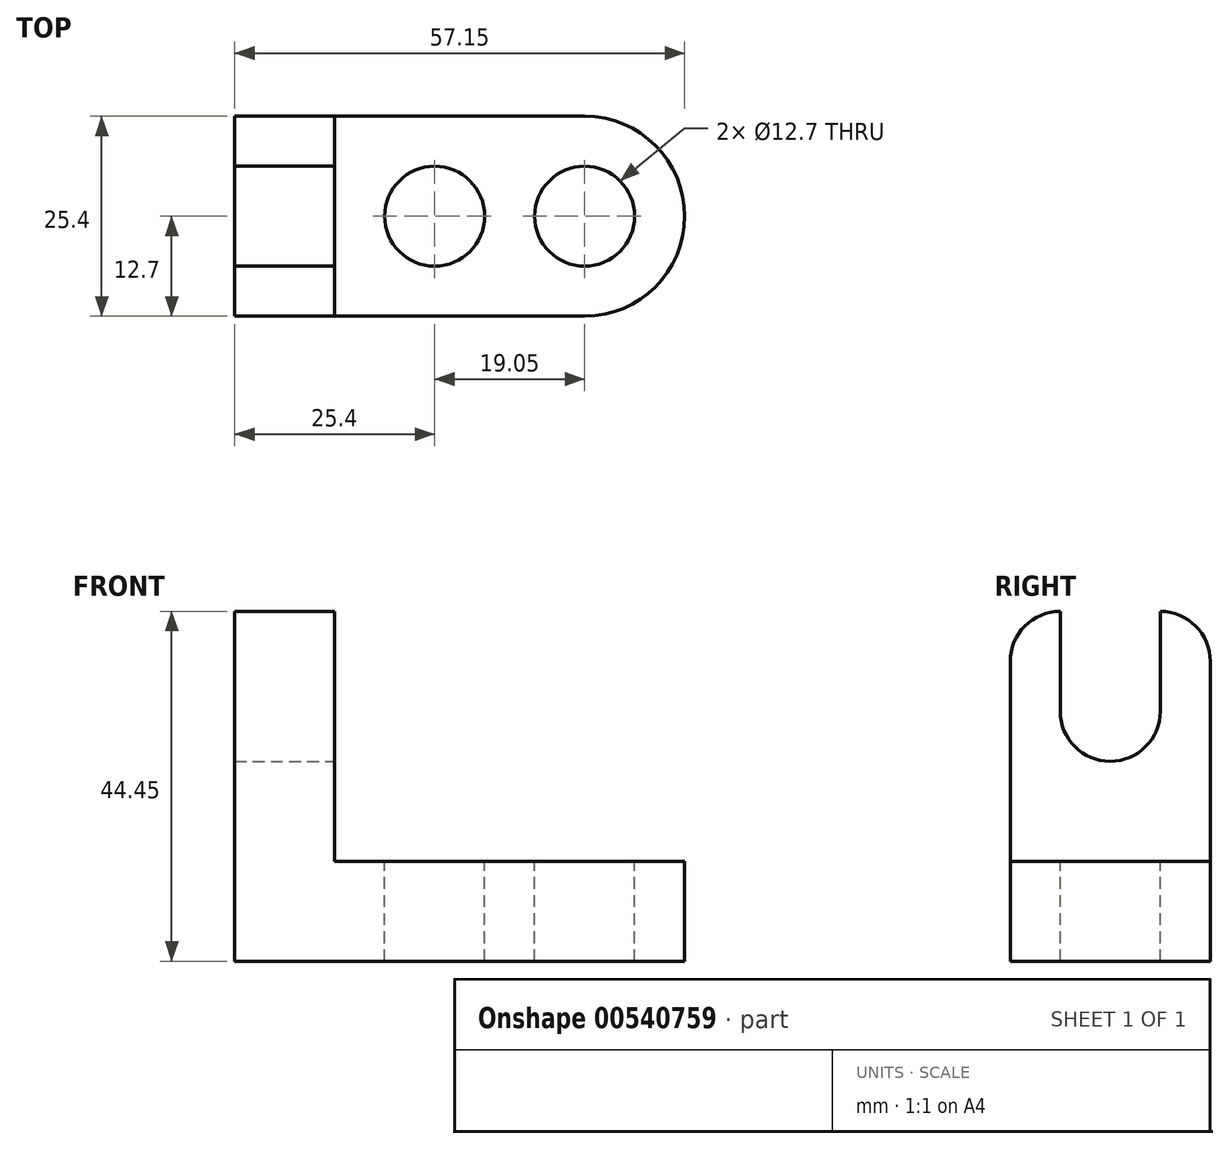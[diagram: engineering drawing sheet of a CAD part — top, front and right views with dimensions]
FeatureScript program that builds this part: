
annotation { "Feature Type Name" : "Feature", "Feature Type Description" : "" }
export const myFeature = defineFeature(function(context is Context, id is Id, definition is map)
    precondition{}
    {
        {
            var Q0;
            Q0=qCreatedBy(makeId("Front.planeOp"),FACE);
            var sketch = newSketch(context, id + "F0", { "sketchPlane" : qUnion([Q0])});
            skLineSegment(sketch, "E0", {"start": v(0, 0) * mm, "end": v(57.15, 0) * mm});
            skLineSegment(sketch, "E1", {"start": v(57.15, 0) * mm, "end": v(57.15, 12.7) * mm});
            skLineSegment(sketch, "E2", {"start": v(57.15, 12.7) * mm, "end": v(12.7, 12.7) * mm});
            skLineSegment(sketch, "E3", {"start": v(12.7, 12.7) * mm, "end": v(12.7, 44.45) * mm});
            skLineSegment(sketch, "E4", {"start": v(12.7, 44.45) * mm, "end": v(0, 44.45) * mm});
            skLineSegment(sketch, "E5", {"start": v(0, 44.45) * mm, "end": v(0, 0) * mm});
            skSolve(sketch);
        }
        {
            var Q0;
            Q0 = qSketchRegion(id + "F0", true);
            extrude(context, id + "F1", {"entities" : qUnion([Q0]), "depth" : 25.4 * mm, "offsetDistance" : 25.4 * mm});
        }
        {
            var Q0;
            Q0=makeQuery(id+"F1.opExtrude","SWEPT_FACE",FACE,{"disambiguationData":[OSD([sQuery(id+"F0.wireOp",EDGE,"E2")])]});
            var sketch = newSketch(context, id + "F2", { "sketchPlane" : qUnion([Q0])});
            skCircle(sketch, "E6", {"center": v(25.4, -12.7) * mm, "radius": 6.35 * mm});
            skCircle(sketch, "E7", {"center": v(44.45, -12.7) * mm, "radius": 6.35 * mm});
            skArc(sketch, "E8", {"start": v(44.45, -25.4) * mm, "mid": v(57.15, -12.7) * mm, "end": v(44.45, 0) * mm});
            skSolve(sketch);
        }
        {
            var Q0;
            Q0=makeQuery(id+"F2.imprint","IMPRINT",FACE,{"disambiguationData":[TD([[makeQuery(id+"F2.imprint","IMPRINT",EDGE,{"derivedFrom":sQuery(id+"F2.wireOp",EDGE,"E6")}),1.0]])]});
            var Q1;
            Q1=makeQuery(id+"F2.imprint","IMPRINT",FACE,{"disambiguationData":[TD([[makeQuery(id+"F2.imprint","IMPRINT",EDGE,{"derivedFrom":sQuery(id+"F2.wireOp",EDGE,"E7")}),1.0]])]});
            var Q2;
            {var subQ0=sQuery(id+"F2.wireOp",EDGE,"E8");var subQ1=sQuery(id+"F0.wireOp",EDGE,"E2");var subQ2=makeQuery(id+"F1.opExtrude","CAP_EDGE",EDGE,{"disambiguationData":[OSD([subQ1])],"isStart":false});var subQ3=makeQuery(id+"F2.imprint","INTERSECT",VERTEX,{"derivedFrom":[subQ2,subQ0]});Q2=makeQuery(id+"F2.imprint","IMPRINT",FACE,{"disambiguationData":[TD([[makeQuery(id+"F2.imprint","IMPRINT",EDGE,{"disambiguationData":[TD([[subQ3,-1.0]])],"derivedFrom":subQ0}),-1.0]])]});}
            var Q3;
            {var subQ0=sQuery(id+"F2.wireOp",EDGE,"E8");var subQ1=sQuery(id+"F0.wireOp",EDGE,"E2");var subQ2=makeQuery(id+"F1.opExtrude","CAP_EDGE",EDGE,{"disambiguationData":[OSD([subQ1])],"isStart":true});var subQ3=makeQuery(id+"F2.imprint","INTERSECT",VERTEX,{"derivedFrom":[subQ2,subQ0]});Q3=makeQuery(id+"F2.imprint","IMPRINT",FACE,{"disambiguationData":[TD([[makeQuery(id+"F2.imprint","IMPRINT",EDGE,{"disambiguationData":[TD([[subQ3,1.0]])],"derivedFrom":subQ0}),-1.0]])]});}
            extrude(context, id + "F3", {"entities" : qUnion([Q0, Q1, Q2, Q3]), "operationType" : NewBodyOperationType.REMOVE, "oppositeDirection" : true, "depth" : 25.4 * mm, "offsetDistance" : 25.4 * mm});
        }
        {
            var Q0;
            Q0=makeQuery(id+"F1.opExtrude","SWEPT_FACE",FACE,{"disambiguationData":[OSD([sQuery(id+"F0.wireOp",EDGE,"E3")])]});
            var sketch = newSketch(context, id + "F4", { "sketchPlane" : qUnion([Q0])});
            skLineSegment(sketch, "E9", {"start": v(-19.05, 44.45) * mm, "end": v(-19.05, 31.75) * mm});
            skLineSegment(sketch, "E10", {"start": v(-6.35, 44.45) * mm, "end": v(-6.35, 31.75) * mm});
            skCircle(sketch, "E11", {"center": v(-12.7, 31.75) * mm, "radius": 6.35 * mm});
            skSolve(sketch);
        }
        {
            var Q0;
            Q0 = qSketchRegion(id + "F4", true);
            var Q1;
            {var subQ0=sQuery(id+"F4.wireOp",EDGE,"E9");Q1=makeQuery(id+"F4.imprint","IMPRINT",FACE,{"disambiguationData":[TD([[makeQuery(id+"F4.imprint","IMPRINT",EDGE,{"derivedFrom":subQ0}),1.0]])]});}
            extrude(context, id + "F5", {"entities" : qUnion([Q0, Q1]), "operationType" : NewBodyOperationType.REMOVE, "oppositeDirection" : true, "depth" : 25.4 * mm, "offsetDistance" : 25.4 * mm});
        }
        {
            var Q0;
            Q0=makeQuery(id+"F1.opExtrude","SWEPT_FACE",FACE,{"disambiguationData":[OSD([sQuery(id+"F0.wireOp",EDGE,"E3")])]});
            var sketch = newSketch(context, id + "F6", { "sketchPlane" : qUnion([Q0])});
            skArc(sketch, "E12", {"start": v(-19.05, 44.45) * mm, "mid": v(-23.54, 42.6) * mm, "end": v(-25.4, 38.1) * mm});
            skPoint(sketch, "E12.endSnap0", {"position": v(-19.05, 38.1) * mm});
            skArc(sketch, "E13", {"start": v(0, 38.1) * mm, "mid": v(-1.86, 42.6) * mm, "end": v(-6.35, 44.45) * mm});
            skSolve(sketch);
        }
        {
            var Q0;
            {var subQ0=sQuery(id+"F6.wireOp",EDGE,"E12");Q0=makeQuery(id+"F6.imprint","IMPRINT",FACE,{"disambiguationData":[TD([[makeQuery(id+"F6.imprint","IMPRINT",EDGE,{"derivedFrom":subQ0}),-1.0]])]});}
            var Q1;
            {var subQ0=sQuery(id+"F6.wireOp",EDGE,"E13");Q1=makeQuery(id+"F6.imprint","IMPRINT",FACE,{"disambiguationData":[TD([[makeQuery(id+"F6.imprint","IMPRINT",EDGE,{"derivedFrom":subQ0}),-1.0]])]});}
            extrude(context, id + "F7", {"entities" : qUnion([Q0, Q1]), "operationType" : NewBodyOperationType.REMOVE, "oppositeDirection" : true, "depth" : 25.4 * mm, "offsetDistance" : 25.4 * mm});
        }
    });
